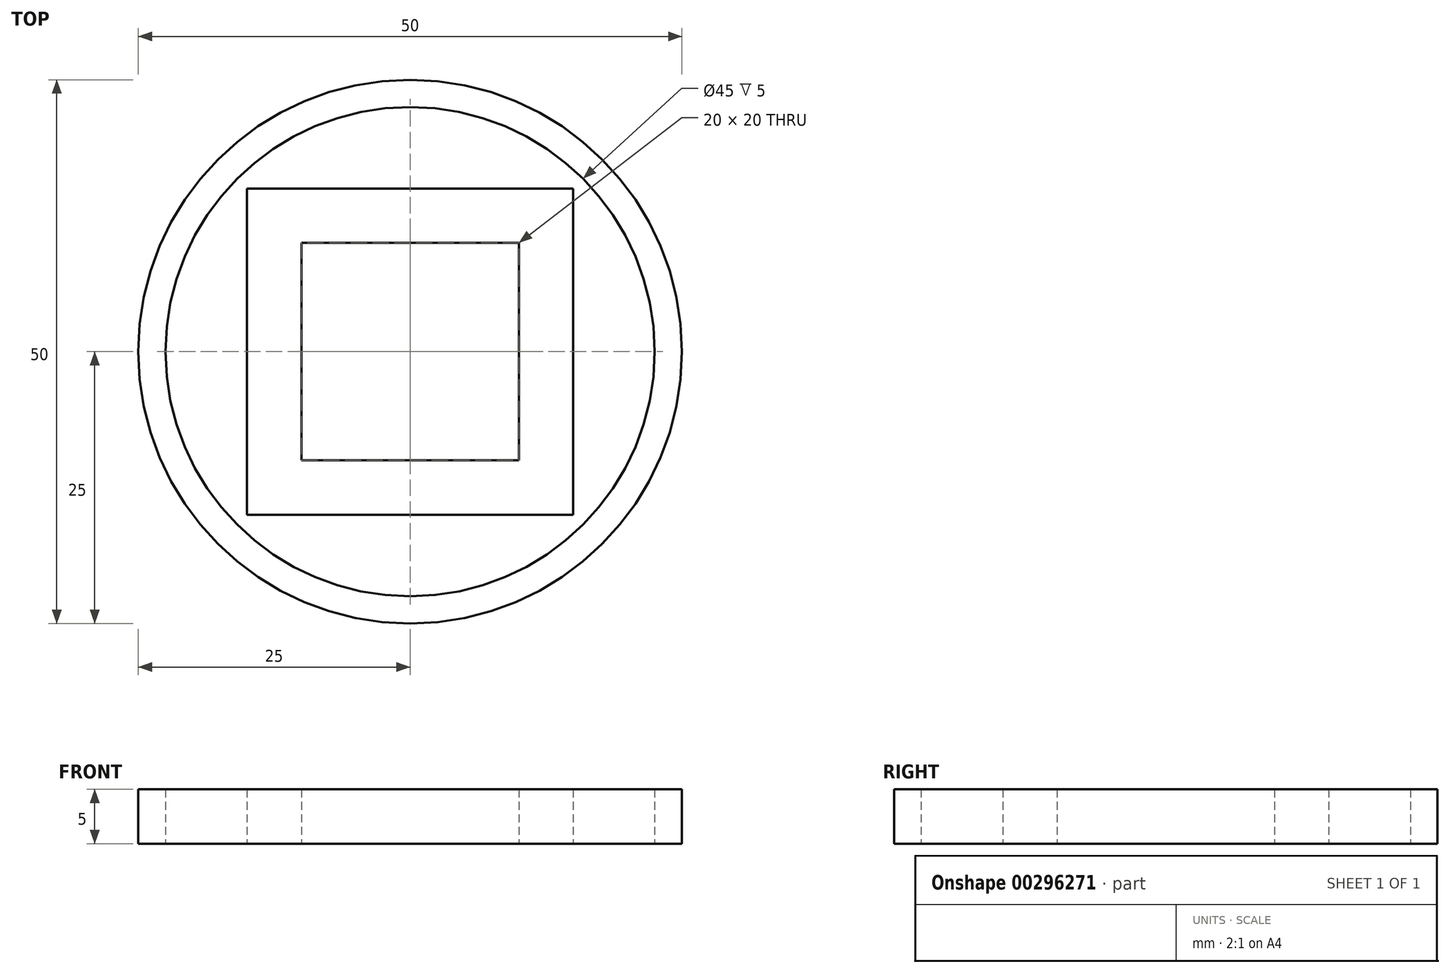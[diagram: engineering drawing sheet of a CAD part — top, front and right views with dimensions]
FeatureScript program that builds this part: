
annotation { "Feature Type Name" : "Feature", "Feature Type Description" : "" }
export const myFeature = defineFeature(function(context is Context, id is Id, definition is map)
    precondition{}
    {
        {
            var Q0;
            Q0=qCreatedBy(makeId("Top.planeOp"),FACE);
            var sketch = newSketch(context, id + "F0", { "sketchPlane" : qUnion([Q0])});
            skCircle(sketch, "E0", {"center": v(0, 0) * mm, "radius": 22.5 * mm});
            skCircle(sketch, "E1", {"center": v(0, 0) * mm, "radius": 25 * mm});
            skSolve(sketch);
        }
        {
            var Q0;
            Q0=makeQuery(id+"F0.imprint","IMPRINT",FACE,{"disambiguationData":[TD([[makeQuery(id+"F0.imprint","IMPRINT",EDGE,{"derivedFrom":sQuery(id+"F0.wireOp",EDGE,"E0")}),-1.0]])]});
            extrude(context, id + "F1", {"entities" : qUnion([Q0]), "depth" : 5 * mm});
        }
        {
            var Q0;
            Q0=makeQuery(id+"F0.imprint","IMPRINT",FACE,{"disambiguationData":[TD([[makeQuery(id+"F0.imprint","IMPRINT",EDGE,{"derivedFrom":sQuery(id+"F0.wireOp",EDGE,"E0")}),-1.0]])]});
            var sketch = newSketch(context, id + "F2", { "sketchPlane" : qUnion([Q0])});
            skLineSegment(sketch, "E2.bottom", {"start": v(-10, -10) * mm, "end": v(10, -10) * mm});
            skLineSegment(sketch, "E2.top", {"start": v(-10, 10) * mm, "end": v(10, 10) * mm});
            skLineSegment(sketch, "E2.left", {"start": v(-10, -10) * mm, "end": v(-10, 10) * mm});
            skLineSegment(sketch, "E2.right", {"start": v(10, -10) * mm, "end": v(10, 10) * mm});
            skPoint(sketch, "E2.middle", {"position": v(0, 0) * mm});
            skLineSegment(sketch, "E3.0", {"start": v(-15, -15) * mm, "end": v(15, -15) * mm});
            skLineSegment(sketch, "E3.1", {"start": v(-15, -15) * mm, "end": v(-15, 15) * mm});
            skLineSegment(sketch, "E3.2", {"start": v(-15, 15) * mm, "end": v(15, 15) * mm});
            skLineSegment(sketch, "E3.3", {"start": v(15, -15) * mm, "end": v(15, 15) * mm});
            skSolve(sketch);
        }
        {
            var Q0;
            Q0=makeQuery(id+"F2.imprint","IMPRINT",FACE,{"disambiguationData":[TD([[makeQuery(id+"F2.imprint","IMPRINT",EDGE,{"derivedFrom":sQuery(id+"F2.wireOp",EDGE,"E3.0")}),1.0]])]});
            var Q1;
            {var subQ0=sQuery(id+"F2.wireOp",EDGE,"E2.left");var subQ1=makeQuery(id+"F0.imprint","IMPRINT",EDGE,{"derivedFrom":sQuery(id+"F0.wireOp",EDGE,"E1")});var subQ2=makeQuery(id+"F2.imprint","INTERSECT",VERTEX,{"disambiguationData":[OD(0.0)],"derivedFrom":[subQ1,subQ0]});Q1=makeQuery(id+"F2.imprint","IMPRINT",FACE,{"disambiguationData":[TD([[makeQuery(id+"F2.imprint","IMPRINT",EDGE,{"disambiguationData":[TD([[subQ2,-1.0]])],"derivedFrom":subQ0}),1.0]])]});}
            var Q2;
            {var subQ0=sQuery(id+"F2.wireOp",EDGE,"E2.bottom");var subQ1=makeQuery(id+"F0.imprint","IMPRINT",EDGE,{"derivedFrom":sQuery(id+"F0.wireOp",EDGE,"E1")});var subQ2=makeQuery(id+"F2.imprint","INTERSECT",VERTEX,{"disambiguationData":[OD(0.0)],"derivedFrom":[subQ1,subQ0]});Q2=makeQuery(id+"F2.imprint","IMPRINT",FACE,{"disambiguationData":[TD([[makeQuery(id+"F2.imprint","IMPRINT",EDGE,{"disambiguationData":[TD([[subQ2,-1.0]])],"derivedFrom":subQ0}),-1.0]])]});}
            var Q3;
            {var subQ0=sQuery(id+"F2.wireOp",EDGE,"E2.right");var subQ1=makeQuery(id+"F0.imprint","IMPRINT",EDGE,{"derivedFrom":sQuery(id+"F0.wireOp",EDGE,"E1")});var subQ2=makeQuery(id+"F2.imprint","INTERSECT",VERTEX,{"disambiguationData":[OD(0.0)],"derivedFrom":[subQ1,subQ0]});Q3=makeQuery(id+"F2.imprint","IMPRINT",FACE,{"disambiguationData":[TD([[makeQuery(id+"F2.imprint","IMPRINT",EDGE,{"disambiguationData":[TD([[subQ2,-1.0]])],"derivedFrom":subQ0}),-1.0]])]});}
            var Q4;
            {var subQ0=sQuery(id+"F2.wireOp",EDGE,"E2.top");var subQ1=makeQuery(id+"F0.imprint","IMPRINT",EDGE,{"derivedFrom":sQuery(id+"F0.wireOp",EDGE,"E1")});var subQ2=makeQuery(id+"F2.imprint","INTERSECT",VERTEX,{"disambiguationData":[OD(0.0)],"derivedFrom":[subQ1,subQ0]});Q4=makeQuery(id+"F2.imprint","IMPRINT",FACE,{"disambiguationData":[TD([[makeQuery(id+"F2.imprint","IMPRINT",EDGE,{"disambiguationData":[TD([[subQ2,-1.0]])],"derivedFrom":subQ0}),1.0]])]});}
            extrude(context, id + "F3", {"entities" : qUnion([Q0, Q1, Q2, Q3, Q4]), "depth" : 5 * mm});
        }
    });
